# Revit family: Vierteaguas T.C-1
name_source: partatom
category: Modelos genéricos
units: mm (PartAtom-declared; Revit-internal decimal feet)

## family parameters
Compartido = No
Corte con vacíos al cargar = No
Cota de conector redondo = Diámetro de uso
Puede alojar armadura = No
Punto de cálculo de habitación = No
Se basa en plano de trabajo = No
Siempre vertical = No
Tipo de pieza = Normal

## types (8) — shared parameters
Descripción = Pieza de hormigón polímero con anclajes de acero inoxidable
Fabricante = ULMA Architectural Solutions
Material = Hormigón polímero STONEO. Color C-1
URL = https://www.ulmaarchitectural.com
zero-valued in all types: Elevación por defecto

## per-type parameters (varying)
| type | Ancho | Ancho doble | Ancho total | Modelo | Visible dos líneas | Visible una linea |
| T20 | 200 mm  [stored 0.656168 ft] | 50 mm  [stored 0.164042 ft] | 235 mm  [stored 0.770997 ft] | Vierteaguas T20 | No | Sí |
| T22 | 220 mm  [stored 0.721785 ft] | 55 mm  [stored 0.180446 ft] | 255 mm  [stored 0.836614 ft] | Vierteaguas T22 | No | Sí |
| T24 | 240 mm  [stored 0.787402 ft] | 60 mm  [stored 0.19685 ft] | 275 mm  [stored 0.902231 ft] | Vierteaguas T24 | No | Sí |
| T26 | 260 mm  [stored 0.853018 ft] | 65 mm  [stored 0.213255 ft] | 295 mm  [stored 0.967848 ft] | Vierteaguas T26 | No | Sí |
| T28 | 280 mm  [stored 0.918635 ft] | 70 mm  [stored 0.229659 ft] | 315 mm  [stored 1.03346 ft] | Vierteaguas T28 | No | Sí |
| T31 | 310 mm  [stored 1.01706 ft] | 78 mm | 345 mm  [stored 1.13189 ft] | Vierteaguas T31 | Sí | No |
| T34 | 340 mm  [stored 1.11549 ft] | 85 mm  [stored 0.278871 ft] | 375 mm  [stored 1.23031 ft] | Vierteaguas L34 | Sí | No |
| T46 | 460 mm  [stored 1.50919 ft] | 115 mm  [stored 0.377297 ft] | 495 mm  [stored 1.62402 ft] | Vierteaguas T46 | Sí | No |

note: column(s) folded — value = type name in every type: Código de montaje

note: [stored X ft] marks values corroborated as IEEE doubles in the binary element streams (Revit-internal decimal feet)
